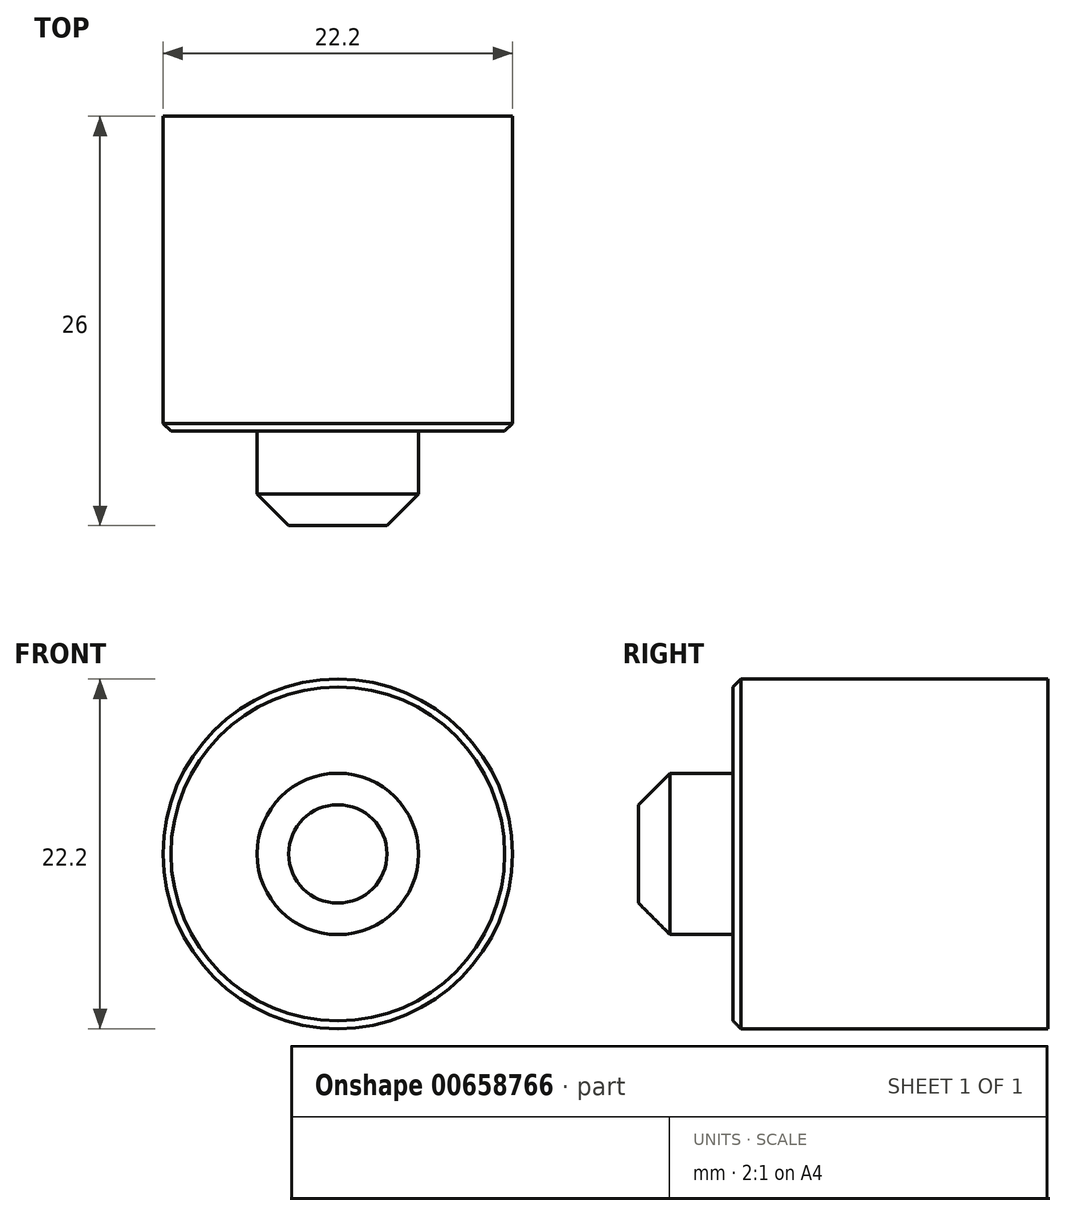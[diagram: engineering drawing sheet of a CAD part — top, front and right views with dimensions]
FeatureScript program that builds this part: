
annotation { "Feature Type Name" : "Feature", "Feature Type Description" : "" }
export const myFeature = defineFeature(function(context is Context, id is Id, definition is map)
    precondition{}
    {
        {
            var Q0;
            Q0=qCreatedBy(makeId("Front.planeOp"),FACE);
            var sketch = newSketch(context, id + "F0", { "sketchPlane" : qUnion([Q0])});
            skCircle(sketch, "E0", {"center": v(0, 0) * mm, "radius": 11.1 * mm});
            skSolve(sketch);
        }
        {
            var Q0;
            Q0=makeQuery(id+"F0.imprint","IMPRINT",FACE,{"disambiguationData":[TD([[makeQuery(id+"F0.imprint","IMPRINT",EDGE,{"derivedFrom":sQuery(id+"F0.wireOp",EDGE,"E0")}),1.0]])]});
            extrude(context, id + "F1", {"entities" : qUnion([Q0]), "depth" : 20 * mm, "offsetDistance" : 25 * mm});
        }
        {
            var Q0;
            Q0=makeQuery(id+"F1.opExtrude","CAP_FACE",FACE,{"disambiguationData":[OSD([sQuery(id+"F0.wireOp",EDGE,"E0")])],"isStart":false});
            var sketch = newSketch(context, id + "F2", { "sketchPlane" : qUnion([Q0])});
            skCircle(sketch, "E1", {"center": v(0, 0) * mm, "radius": 5.12 * mm});
            skSolve(sketch);
        }
        {
            var Q0;
            Q0=makeQuery(id+"F2.imprint","IMPRINT",FACE,{"disambiguationData":[TD([[makeQuery(id+"F2.imprint","IMPRINT",EDGE,{"derivedFrom":sQuery(id+"F2.wireOp",EDGE,"E1")}),1.0]])]});
            extrude(context, id + "F3", {"entities" : qUnion([Q0]), "operationType" : NewBodyOperationType.ADD, "depth" : 6 * mm, "offsetDistance" : 25 * mm});
        }
        {
            var Q0;
            Q0=makeQuery(id+"F3.opExtrude","CAP_EDGE",EDGE,{"disambiguationData":[OSD([sQuery(id+"F2.wireOp",EDGE,"E1")])],"isStart":false});
            chamfer(context, id + "F4", {"entities" : qUnion([Q0]), "width" : 2 * mm, "tangentPropagation" : true});
        }
        {
            var Q0;
            Q0=makeQuery(id+"F1.opExtrude","CAP_EDGE",EDGE,{"disambiguationData":[OSD([sQuery(id+"F0.wireOp",EDGE,"E0")])],"isStart":false});
            chamfer(context, id + "F5", {"entities" : qUnion([Q0]), "width" : 0.5 * mm, "tangentPropagation" : true});
        }
    });
